# Revit family: Storage-Mounted-Teknion-JNBP-Suspended_Pedestal_File_Drawer-R2015
name_source: partatom
category: Furniture
revit_build: Autodesk Revit Architecture 2015 (Build: 20140323_1530(x64)
units: mm (PartAtom-declared; Revit-internal decimal feet)

## types (2) — shared parameters
Assembly Code = E2020200
Description = Suspended Pedestal – File Drawer
Manufacturer = Teknion
Manufacturer Fax = 416.661.4586
Model = JNBP
Part Number = JNBP
Product Documentation Link = http://www.teknion.com
Product Line = Expansion Cityline
Product Page URL = http://www.teknion.com
Series = Expansion Cityline
Sustainability Data = http://www.teknion.com
URL = www.teknion.com
Unit Weight URL = http://www.teknion.com
Warranty = http://www.teknion.com

## per-type parameters (varying)
| type | Front Finish | Has Metal Front Style | Has Solid Front Style |
| Metal | Mica - Teknion - V - Satin - Very White | Yes | No |
| Solid | Source Laminate - Teknion - XS - Storm White | No | Yes |

## geometry (parser evidence)
native form markers: Blend x2, Sweep x1
no freeform markers — native parametric forms only
